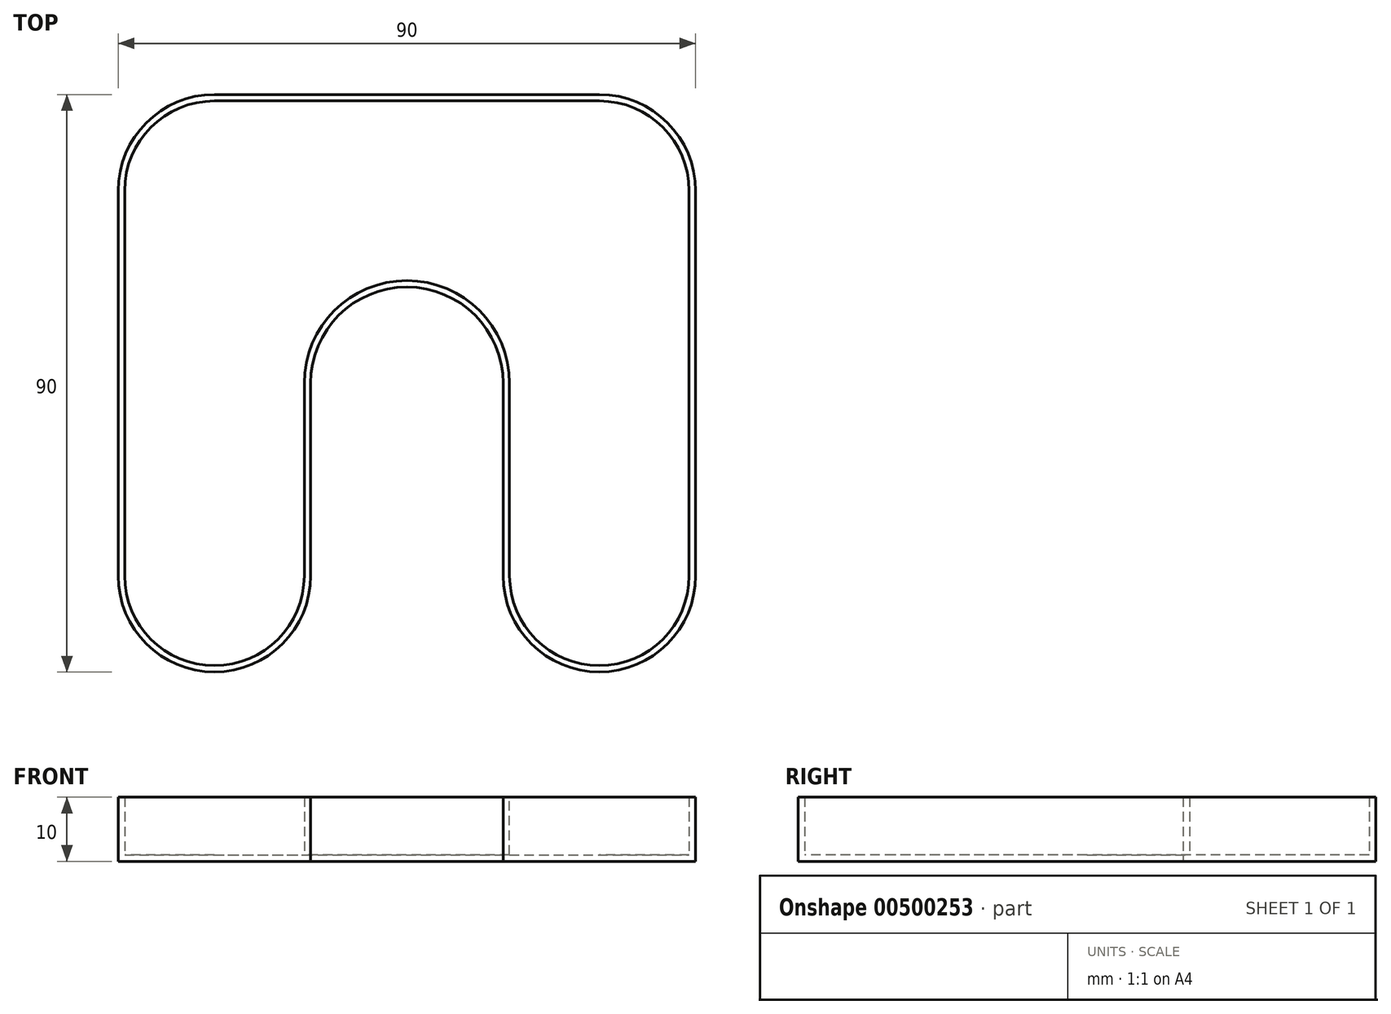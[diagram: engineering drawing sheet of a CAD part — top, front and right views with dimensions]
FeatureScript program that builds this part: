
annotation { "Feature Type Name" : "Feature", "Feature Type Description" : "" }
export const myFeature = defineFeature(function(context is Context, id is Id, definition is map)
    precondition{}
    {
        {
            var Q0;
            Q0=qCreatedBy(makeId("Top.planeOp"),FACE);
            var sketch = newSketch(context, id + "F0", { "sketchPlane" : qUnion([Q0])});
            skLineSegment(sketch, "E0.bottom", {"start": v(-42.3, 31.98) * mm, "end": v(17.7, 31.98) * mm});
            skLineSegment(sketch, "E0.top", {"start": v(-42.3, -58.02) * mm, "end": v(-42.3, -58.02) * mm});
            skLineSegment(sketch, "E0.left", {"start": v(-57.3, 16.98) * mm, "end": v(-57.3, -43.02) * mm});
            skLineSegment(sketch, "E0.right", {"start": v(32.7, 16.98) * mm, "end": v(32.7, -43.02) * mm});
            skLineSegment(sketch, "E1", {"start": v(-27.3, -13.02) * mm, "end": v(-27.3, -43.02) * mm});
            skLineSegment(sketch, "E2", {"start": v(-12.3, 1.98) * mm, "end": v(-12.3, 1.98) * mm});
            skLineSegment(sketch, "E3", {"start": v(2.7, -13.02) * mm, "end": v(2.7, -43.02) * mm});
            skLineSegment(sketch, "E4.trimOffspring", {"start": v(17.7, -58.02) * mm, "end": v(17.7, -58.02) * mm});
            skPoint(sketch, "E5.visualSharp", {"position": v(-57.3, 31.98) * mm});
            skArc(sketch, "E5.filletArc", {"start": v(-42.3, 31.98) * mm, "mid": v(-52.9, 27.6) * mm, "end": v(-57.3, 16.98) * mm});
            skPoint(sketch, "E6.visualSharp", {"position": v(32.7, 31.98) * mm});
            skArc(sketch, "E6.filletArc", {"start": v(32.7, 16.98) * mm, "mid": v(28.32, 27.6) * mm, "end": v(17.7, 31.98) * mm});
            skPoint(sketch, "E7.visualSharp", {"position": v(32.7, -58.02) * mm});
            skArc(sketch, "E7.filletArc", {"start": v(17.7, -58.02) * mm, "mid": v(28.32, -53.62) * mm, "end": v(32.7, -43.02) * mm});
            skPoint(sketch, "E8.visualSharp", {"position": v(-27.3, 1.98) * mm});
            skArc(sketch, "E8.filletArc", {"start": v(-12.3, 1.98) * mm, "mid": v(-22.9, -2.4) * mm, "end": v(-27.3, -13.02) * mm});
            skPoint(sketch, "E9.visualSharp", {"position": v(2.7, 1.98) * mm});
            skArc(sketch, "E9.filletArc", {"start": v(2.7, -13.02) * mm, "mid": v(-1.68, -2.4) * mm, "end": v(-12.3, 1.98) * mm});
            skPoint(sketch, "E10.visualSharp", {"position": v(-57.3, -58.02) * mm});
            skArc(sketch, "E10.filletArc", {"start": v(-57.3, -43.02) * mm, "mid": v(-52.9, -53.62) * mm, "end": v(-42.3, -58.02) * mm});
            skPoint(sketch, "E11.visualSharp", {"position": v(-27.3, -58.02) * mm});
            skArc(sketch, "E11.filletArc", {"start": v(-42.3, -58.02) * mm, "mid": v(-31.68, -53.62) * mm, "end": v(-27.3, -43.02) * mm});
            skPoint(sketch, "E12.visualSharp", {"position": v(2.7, -58.02) * mm});
            skArc(sketch, "E12.filletArc", {"start": v(2.7, -43.02) * mm, "mid": v(7.1, -53.62) * mm, "end": v(17.7, -58.02) * mm});
            skSolve(sketch);
        }
        {
            var Q0;
            Q0=makeQuery(id+"F0.imprint","IMPRINT",FACE,{"disambiguationData":[TD([[makeQuery(id+"F0.imprint","IMPRINT",EDGE,{"derivedFrom":sQuery(id+"F0.wireOp",EDGE,"E0.bottom")}),-1.0]])]});
            extrude(context, id + "F1", {"entities" : qUnion([Q0]), "depth" : 10 * mm});
        }
        {
            var Q0;
            Q0=makeQuery(id+"F1.opExtrude","CAP_FACE",FACE,{"disambiguationData":[OSD([sQuery(id+"F0.wireOp",EDGE,"E0.bottom"),sQuery(id+"F0.wireOp",EDGE,"E0.left"),sQuery(id+"F0.wireOp",EDGE,"E0.right"),sQuery(id+"F0.wireOp",EDGE,"E1"),sQuery(id+"F0.wireOp",EDGE,"E3"),sQuery(id+"F0.wireOp",EDGE,"E5.filletArc"),sQuery(id+"F0.wireOp",EDGE,"E6.filletArc"),sQuery(id+"F0.wireOp",EDGE,"E7.filletArc"),sQuery(id+"F0.wireOp",EDGE,"E8.filletArc"),sQuery(id+"F0.wireOp",EDGE,"E9.filletArc"),sQuery(id+"F0.wireOp",EDGE,"E10.filletArc"),sQuery(id+"F0.wireOp",EDGE,"E11.filletArc"),sQuery(id+"F0.wireOp",EDGE,"E12.filletArc")])],"isStart":false});
            shell(context, id + "F2", {"entities" : qUnion([Q0]), "thickness" : 1 * mm});
        }
    });
